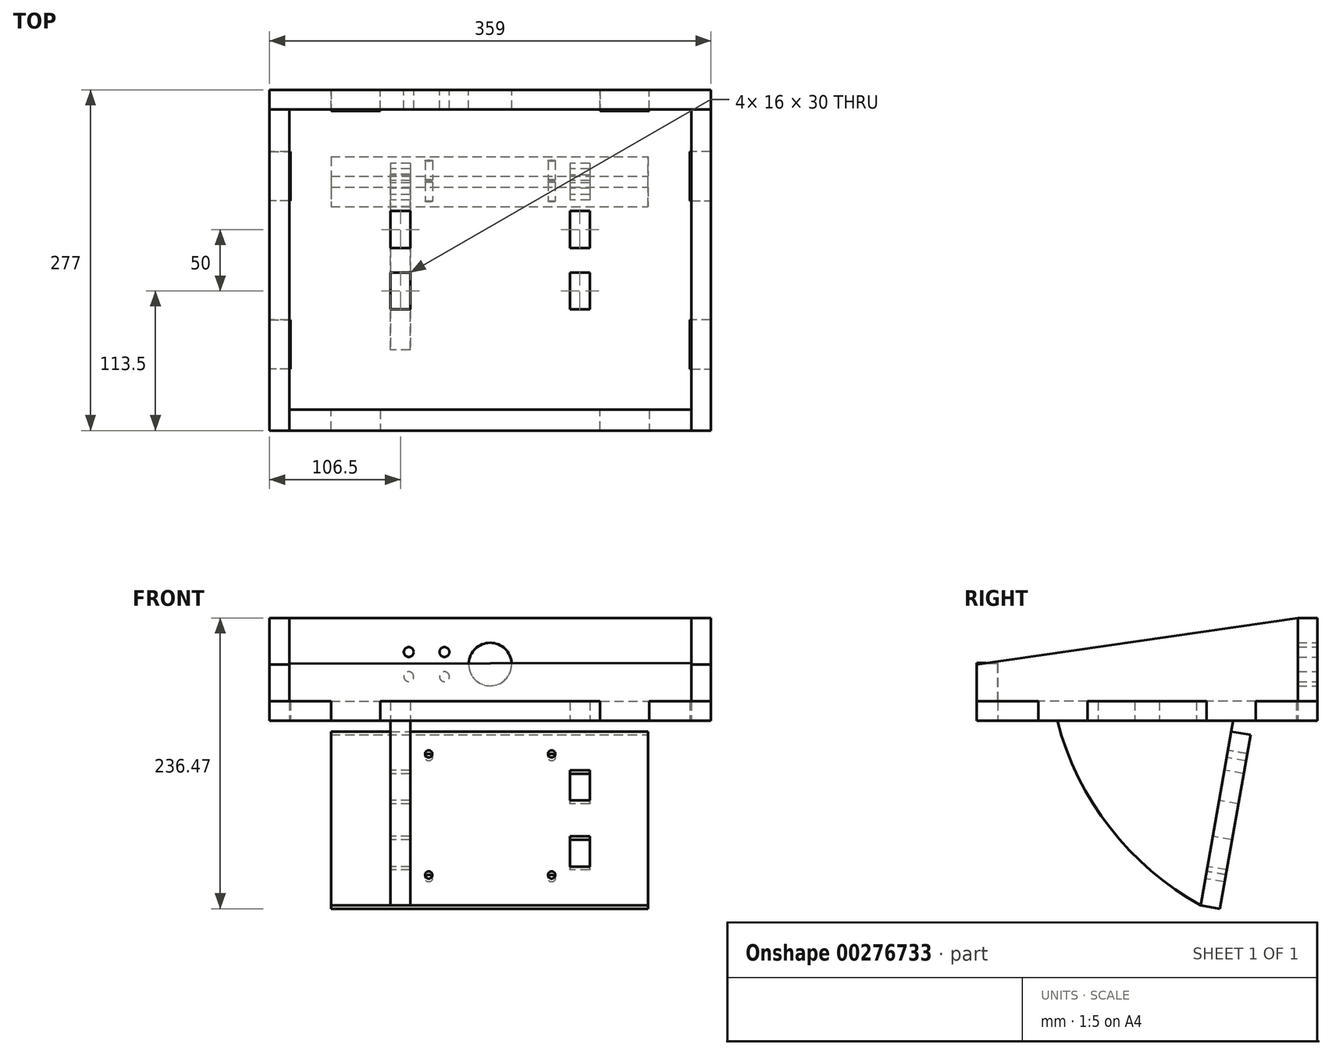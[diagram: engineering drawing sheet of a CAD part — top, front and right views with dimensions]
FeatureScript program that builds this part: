
annotation { "Feature Type Name" : "Feature", "Feature Type Description" : "" }
export const myFeature = defineFeature(function(context is Context, id is Id, definition is map)
    precondition{}
    {
        {
            var Q0;
            Q0=qCreatedBy(makeId("Top.planeOp"),FACE);
            var sketch = newSketch(context, id + "F0", { "sketchPlane" : qUnion([Q0])});
            skLineSegment(sketch, "E0.bottom", {"start": v(179.5, -138.5) * mm, "end": v(-179.5, -138.5) * mm});
            skLineSegment(sketch, "E0.top", {"start": v(179.5, 138.5) * mm, "end": v(-179.5, 138.5) * mm});
            skLineSegment(sketch, "E0.left", {"start": v(179.5, -138.5) * mm, "end": v(179.5, 138.5) * mm});
            skLineSegment(sketch, "E0.right", {"start": v(-179.5, -138.5) * mm, "end": v(-179.5, 138.5) * mm});
            skPoint(sketch, "E0.middle", {"position": v(0, 0) * mm});
            skLineSegment(sketch, "E1.bottom", {"start": v(-179.5, 138.5) * mm, "end": v(-163.5, 138.5) * mm, "construction": true});
            skLineSegment(sketch, "E1.top", {"start": v(-179.5, -138.5) * mm, "end": v(-162.5, -138.5) * mm, "construction": true});
            skLineSegment(sketch, "E1.left", {"start": v(-179.5, 138.5) * mm, "end": v(-179.5, -138.5) * mm, "construction": true});
            skLineSegment(sketch, "E2.top", {"start": v(-179.5, -138.5) * mm, "end": v(179.5, -138.5) * mm, "construction": true});
            skLineSegment(sketch, "E2.left", {"start": v(-179.5, -121.5) * mm, "end": v(-179.5, -138.5) * mm, "construction": true});
            skLineSegment(sketch, "E2.right", {"start": v(179.5, -121.5) * mm, "end": v(179.5, -138.5) * mm, "construction": true});
            skLineSegment(sketch, "E3.bottom", {"start": v(179.5, 138.5) * mm, "end": v(162.5, 138.5) * mm, "construction": true});
            skLineSegment(sketch, "E3.top", {"start": v(179.5, -138.5) * mm, "end": v(162.5, -138.5) * mm, "construction": true});
            skLineSegment(sketch, "E3.left", {"start": v(179.5, 138.5) * mm, "end": v(179.5, -138.5) * mm, "construction": true});
            skLineSegment(sketch, "E4.bottom", {"start": v(-179.5, 138.5) * mm, "end": v(179.5, 138.5) * mm, "construction": true});
            skLineSegment(sketch, "E4.left", {"start": v(-179.5, 138.5) * mm, "end": v(-179.5, 122.5) * mm, "construction": true});
            skLineSegment(sketch, "E4.right", {"start": v(179.5, 138.5) * mm, "end": v(179.5, 121.5) * mm, "construction": true});
            skLineSegment(sketch, "E5", {"start": v(-179.5, 88.5) * mm, "end": v(-162.5, 88.5) * mm});
            skLineSegment(sketch, "E6", {"start": v(-162.5, 88.5) * mm, "end": v(-162.5, 48.5) * mm});
            skLineSegment(sketch, "E7", {"start": v(-162.5, 48.5) * mm, "end": v(-179.5, 48.5) * mm});
            skLineSegment(sketch, "E8", {"start": v(-179.5, -48.5) * mm, "end": v(-162.5, -48.5) * mm});
            skLineSegment(sketch, "E9", {"start": v(-162.5, -48.5) * mm, "end": v(-162.5, -88.5) * mm});
            skLineSegment(sketch, "E10", {"start": v(-162.5, -88.5) * mm, "end": v(-179.5, -88.5) * mm});
            skLineSegment(sketch, "E11", {"start": v(-129.5, -138.5) * mm, "end": v(-129.5, -121.5) * mm});
            skLineSegment(sketch, "E12", {"start": v(-129.5, -121.5) * mm, "end": v(-89.5, -121.5) * mm});
            skLineSegment(sketch, "E13", {"start": v(-89.5, -121.5) * mm, "end": v(-89.5, -138.5) * mm});
            skLineSegment(sketch, "E14", {"start": v(89.5, -138.5) * mm, "end": v(89.5, -121.5) * mm});
            skLineSegment(sketch, "E15", {"start": v(89.5, -121.5) * mm, "end": v(129.5, -121.5) * mm});
            skLineSegment(sketch, "E16", {"start": v(129.5, -121.5) * mm, "end": v(129.5, -138.5) * mm});
            skLineSegment(sketch, "E17", {"start": v(-129.5, 138.5) * mm, "end": v(-129.5, 121.5) * mm});
            skLineSegment(sketch, "E18", {"start": v(-129.5, 121.5) * mm, "end": v(-89.5, 121.5) * mm});
            skLineSegment(sketch, "E19", {"start": v(-89.5, 121.5) * mm, "end": v(-89.5, 138.5) * mm});
            skLineSegment(sketch, "E20", {"start": v(89.5, 138.5) * mm, "end": v(89.5, 121.5) * mm});
            skLineSegment(sketch, "E21", {"start": v(89.5, 121.5) * mm, "end": v(129.5, 121.5) * mm});
            skLineSegment(sketch, "E22", {"start": v(129.5, 121.5) * mm, "end": v(129.5, 138.5) * mm});
            skLineSegment(sketch, "E23", {"start": v(179.5, 88.5) * mm, "end": v(162.5, 88.5) * mm});
            skLineSegment(sketch, "E24", {"start": v(162.5, 88.5) * mm, "end": v(162.5, 48.5) * mm});
            skLineSegment(sketch, "E25", {"start": v(162.5, 48.5) * mm, "end": v(179.5, 48.5) * mm});
            skLineSegment(sketch, "E26", {"start": v(179.5, -48.5) * mm, "end": v(162.5, -48.5) * mm});
            skLineSegment(sketch, "E27", {"start": v(162.5, -48.5) * mm, "end": v(162.5, -88.5) * mm});
            skLineSegment(sketch, "E28", {"start": v(162.5, -88.5) * mm, "end": v(179.5, -88.5) * mm});
            skSolve(sketch);
        }
        {
            var Q0;
            {var subQ11=sQuery(id+"F0.wireOp",EDGE,"E5");Q0=makeQuery(id+"F0.imprint","IMPRINT",FACE,{"disambiguationData":[TD([[makeQuery(id+"F0.imprint","IMPRINT",EDGE,{"derivedFrom":subQ11}),1.0]])]});}
            extrude(context, id + "F1", {"entities" : qUnion([Q0]), "depth" : 16 * mm});
        }
        {
            var Q0;
            {var subQ0=sQuery(id+"F0.wireOp",EDGE,"E0.right");Q0=makeQuery(id+"F1.opExtrude","SWEPT_FACE",FACE,{"disambiguationData":[OSD([subQ0]),TDD([makeQuery(id+"F0.imprint","IMPRINT",EDGE,{"disambiguationData":[TD([[makeQuery(id+"F0.imprint","INTERSECT",VERTEX,{"derivedFrom":[sQuery(id+"F0.wireOp",EDGE,"E0.top"),subQ0]}),1.0]])],"derivedFrom":subQ0})])]});}
            var sketch = newSketch(context, id + "F2", { "sketchPlane" : qUnion([Q0])});
            skLineSegment(sketch, "E29.bottom", {"start": v(-138.5, 0) * mm, "end": v(138.5, 0) * mm});
            skLineSegment(sketch, "E29.top", {"start": v(-138.5, 86) * mm, "end": v(138.5, 86) * mm});
            skLineSegment(sketch, "E29.left", {"start": v(-138.5, 0) * mm, "end": v(-138.5, 86) * mm});
            skLineSegment(sketch, "E29.right", {"start": v(138.5, 0) * mm, "end": v(138.5, 86) * mm});
            skLineSegment(sketch, "E30", {"start": v(-88.5, 0) * mm, "end": v(-88.5, 16) * mm});
            skLineSegment(sketch, "E31", {"start": v(-88.5, 16) * mm, "end": v(-48.5, 16) * mm});
            skLineSegment(sketch, "E32", {"start": v(-48.5, 16) * mm, "end": v(-48.5, 0) * mm});
            skLineSegment(sketch, "E33", {"start": v(48.5, 0) * mm, "end": v(48.5, 16) * mm});
            skLineSegment(sketch, "E34", {"start": v(48.5, 16) * mm, "end": v(88.5, 16) * mm});
            skLineSegment(sketch, "E35", {"start": v(88.5, 16) * mm, "end": v(88.5, 0) * mm});
            skLineSegment(sketch, "E36", {"start": v(-88.5, 16) * mm, "end": v(-138.5, 16) * mm});
            skLineSegment(sketch, "E37", {"start": v(-138.5, 16) * mm, "end": v(-138.5, 0) * mm});
            skLineSegment(sketch, "E38", {"start": v(-48.5, 16) * mm, "end": v(48.5, 16) * mm});
            skLineSegment(sketch, "E39", {"start": v(48.5, 0) * mm, "end": v(-48.5, 0) * mm});
            skLineSegment(sketch, "E40", {"start": v(88.5, 16) * mm, "end": v(138.5, 16) * mm});
            skLineSegment(sketch, "E41", {"start": v(138.5, 16) * mm, "end": v(138.5, 0) * mm});
            skLineSegment(sketch, "E42", {"start": v(-138.5, 86) * mm, "end": v(138.5, 46) * mm});
            skLineSegment(sketch, "E43", {"start": v(-122.5, 86) * mm, "end": v(-122.5, 83.69) * mm});
            skLineSegment(sketch, "E44", {"start": v(-122.5, 83.69) * mm, "end": v(-122.5, 16) * mm});
            skSolve(sketch);
        }
        {
            var Q0;
            {var subQ0=sQuery(id+"F2.wireOp",EDGE,"E30");Q0=makeQuery(id+"F2.imprint","IMPRINT",FACE,{"disambiguationData":[TD([[makeQuery(id+"F2.imprint","IMPRINT",EDGE,{"derivedFrom":subQ0}),1.0]])]});}
            var Q1;
            {var subQ0=sQuery(id+"F2.wireOp",EDGE,"E33");Q1=makeQuery(id+"F2.imprint","IMPRINT",FACE,{"disambiguationData":[TD([[makeQuery(id+"F2.imprint","IMPRINT",EDGE,{"derivedFrom":subQ0}),-1.0]])]});}
            var Q2;
            {var subQ0=sQuery(id+"F2.wireOp",EDGE,"E31");Q2=makeQuery(id+"F2.imprint","IMPRINT",FACE,{"disambiguationData":[TD([[makeQuery(id+"F2.imprint","IMPRINT",EDGE,{"derivedFrom":subQ0}),1.0]])]});}
            extrude(context, id + "F3", {"entities" : qUnion([Q0, Q1, Q2]), "oppositeDirection" : true, "depth" : 16 * mm});
        }
        {
            var Q0;
            {var subQ0=sQuery(id+"F0.wireOp",EDGE,"E0.top");Q0=makeQuery(id+"F1.opExtrude","SWEPT_FACE",FACE,{"disambiguationData":[OSD([subQ0]),TDD([makeQuery(id+"F0.imprint","IMPRINT",EDGE,{"disambiguationData":[TD([[makeQuery(id+"F0.imprint","INTERSECT",VERTEX,{"derivedFrom":[subQ0,sQuery(id+"F0.wireOp",EDGE,"E0.left")]}),-1.0]])],"derivedFrom":subQ0})])]});}
            var sketch = newSketch(context, id + "F4", { "sketchPlane" : qUnion([Q0])});
            skLineSegment(sketch, "E45", {"start": v(179.5, 16) * mm, "end": v(129.5, 16) * mm});
            skLineSegment(sketch, "E46", {"start": v(129.5, 16) * mm, "end": v(129.5, 0) * mm});
            skLineSegment(sketch, "E47", {"start": v(129.5, 0) * mm, "end": v(89.35, 0) * mm});
            skLineSegment(sketch, "E48", {"start": v(89.35, 0) * mm, "end": v(89.35, 16) * mm});
            skLineSegment(sketch, "E49", {"start": v(89.35, 16) * mm, "end": v(-89.5, 16) * mm});
            skLineSegment(sketch, "E50", {"start": v(-89.5, 16) * mm, "end": v(-89.5, 0) * mm});
            skLineSegment(sketch, "E51", {"start": v(-89.5, 0) * mm, "end": v(-129.5, 0) * mm});
            skLineSegment(sketch, "E52", {"start": v(-129.5, 0) * mm, "end": v(-129.5, 16) * mm});
            skLineSegment(sketch, "E53", {"start": v(-129.5, 16) * mm, "end": v(-179.5, 16) * mm});
            skLineSegment(sketch, "E54", {"start": v(-179.5, 16) * mm, "end": v(-179.5, 83.69) * mm});
            skLineSegment(sketch, "E55", {"start": v(-179.5, 83.69) * mm, "end": v(179.5, 83.69) * mm});
            skLineSegment(sketch, "E56", {"start": v(179.5, 83.69) * mm, "end": v(179.5, 16) * mm});
            skSolve(sketch);
        }
        {
            var Q0;
            Q0=makeQuery(id+"F4.imprint","IMPRINT",FACE,{"disambiguationData":[TD([[makeQuery(id+"F4.imprint","IMPRINT",EDGE,{"derivedFrom":sQuery(id+"F4.wireOp",EDGE,"E45")}),-1.0]])]});
            extrude(context, id + "F5", {"entities" : qUnion([Q0]), "oppositeDirection" : true, "depth" : 16 * mm});
        }
        {
            var Q0;
            {var subQ0=sQuery(id+"F0.wireOp",EDGE,"E0.left");Q0=makeQuery(id+"F1.opExtrude","SWEPT_FACE",FACE,{"disambiguationData":[OSD([subQ0]),TDD([makeQuery(id+"F0.imprint","IMPRINT",EDGE,{"disambiguationData":[TD([[makeQuery(id+"F0.imprint","INTERSECT",VERTEX,{"derivedFrom":[sQuery(id+"F0.wireOp",EDGE,"E0.bottom"),subQ0]}),-1.0]])],"derivedFrom":subQ0})])]});}
            var sketch = newSketch(context, id + "F6", { "sketchPlane" : qUnion([Q0])});
            skLineSegment(sketch, "E57", {"start": v(-138.5, 16) * mm, "end": v(-138.5, 46) * mm});
            skLineSegment(sketch, "E58", {"start": v(-88.5, 16) * mm, "end": v(-88.5, 0) * mm});
            skLineSegment(sketch, "E59", {"start": v(-88.5, 0) * mm, "end": v(-48.5, 0) * mm});
            skLineSegment(sketch, "E60", {"start": v(-48.5, 0) * mm, "end": v(-48.5, 16) * mm});
            skLineSegment(sketch, "E61", {"start": v(-48.5, 16) * mm, "end": v(48.5, 16) * mm});
            skLineSegment(sketch, "E62", {"start": v(48.5, 16) * mm, "end": v(48.5, 0) * mm});
            skLineSegment(sketch, "E63", {"start": v(48.5, 0) * mm, "end": v(88.5, 0) * mm});
            skLineSegment(sketch, "E64", {"start": v(88.5, 0) * mm, "end": v(88.5, 16) * mm});
            skLineSegment(sketch, "E65", {"start": v(88.5, 16) * mm, "end": v(122.5, 16) * mm});
            skLineSegment(sketch, "E66", {"start": v(122.5, 16) * mm, "end": v(122.5, 83.69) * mm});
            skLineSegment(sketch, "E67", {"start": v(122.5, 83.69) * mm, "end": v(-138.5, 46) * mm});
            skSolve(sketch);
        }
        {
            var Q0;
            Q0=makeQuery(id+"F6.imprint","IMPRINT",FACE,{"disambiguationData":[TD([[makeQuery(id+"F6.imprint","IMPRINT",EDGE,{"derivedFrom":sQuery(id+"F6.wireOp",EDGE,"E57")}),-1.0]])]});
            extrude(context, id + "F7", {"entities" : qUnion([Q0]), "oppositeDirection" : true, "depth" : 16 * mm});
        }
        {
            var Q0;
            {var subQ0=sQuery(id+"F0.wireOp",EDGE,"E0.bottom");Q0=makeQuery(id+"F1.opExtrude","SWEPT_FACE",FACE,{"disambiguationData":[OSD([subQ0]),TDD([makeQuery(id+"F0.imprint","IMPRINT",EDGE,{"disambiguationData":[TD([[makeQuery(id+"F0.imprint","INTERSECT",VERTEX,{"derivedFrom":[subQ0,sQuery(id+"F0.wireOp",EDGE,"E0.right")]}),1.0]])],"derivedFrom":subQ0})])]});}
            var sketch = newSketch(context, id + "F8", { "sketchPlane" : qUnion([Q0])});
            skLineSegment(sketch, "E68", {"start": v(-163.5, 46.6) * mm, "end": v(-163.5, 16) * mm});
            skLineSegment(sketch, "E69", {"start": v(-163.5, 16) * mm, "end": v(-129.5, 16) * mm});
            skLineSegment(sketch, "E70", {"start": v(-129.5, 16) * mm, "end": v(-129.5, 0) * mm});
            skLineSegment(sketch, "E71", {"start": v(-129.5, 0) * mm, "end": v(-89.5, 0) * mm});
            skLineSegment(sketch, "E72", {"start": v(-89.5, 0) * mm, "end": v(-89.5, 16) * mm});
            skLineSegment(sketch, "E73", {"start": v(-89.5, 16) * mm, "end": v(89.5, 16) * mm});
            skLineSegment(sketch, "E74", {"start": v(89.5, 16) * mm, "end": v(89.5, 0) * mm});
            skLineSegment(sketch, "E75", {"start": v(89.5, 0) * mm, "end": v(129.5, 0) * mm});
            skLineSegment(sketch, "E76", {"start": v(129.5, 0) * mm, "end": v(129.5, 16) * mm});
            skLineSegment(sketch, "E77", {"start": v(129.5, 16) * mm, "end": v(163.5, 16) * mm});
            skLineSegment(sketch, "E78", {"start": v(163.5, 16) * mm, "end": v(163.5, 47.06) * mm});
            skLineSegment(sketch, "E79", {"start": v(163.5, 47.06) * mm, "end": v(-163.5, 46.6) * mm});
            skSolve(sketch);
        }
        {
            var Q0;
            Q0 = qSketchRegion(id + "F8", true);
            extrude(context, id + "F9", {"entities" : qUnion([Q0]), "oppositeDirection" : true, "depth" : 17 * mm});
        }
        {
            var Q0;
            Q0=makeQuery(id+"F5.opExtrude","CAP_FACE",FACE,{"disambiguationData":[OSD([sQuery(id+"F4.wireOp",EDGE,"E45"),sQuery(id+"F4.wireOp",EDGE,"E46"),sQuery(id+"F4.wireOp",EDGE,"E47"),sQuery(id+"F4.wireOp",EDGE,"E48"),sQuery(id+"F4.wireOp",EDGE,"E49"),sQuery(id+"F4.wireOp",EDGE,"E50"),sQuery(id+"F4.wireOp",EDGE,"E51"),sQuery(id+"F4.wireOp",EDGE,"E52"),sQuery(id+"F4.wireOp",EDGE,"E53"),sQuery(id+"F4.wireOp",EDGE,"E54"),sQuery(id+"F4.wireOp",EDGE,"E55"),sQuery(id+"F4.wireOp",EDGE,"E56")])],"isStart":true});
            var sketch = newSketch(context, id + "F10", { "sketchPlane" : qUnion([Q0])});
            skCircle(sketch, "E80", {"center": v(0, 46) * mm, "radius": 17.5 * mm});
            skCircle(sketch, "E81", {"center": v(37.22, 56) * mm, "radius": 4 * mm});
            skCircle(sketch, "E82", {"center": v(37.22, 36) * mm, "radius": 4 * mm});
            skCircle(sketch, "E83", {"center": v(66.21, 56) * mm, "radius": 4 * mm});
            skCircle(sketch, "E84", {"center": v(66.21, 36) * mm, "radius": 4 * mm});
            skLineSegment(sketch, "E85", {"start": v(0, 46) * mm, "end": v(95.92, 46) * mm, "construction": true});
            skSolve(sketch);
        }
        {
            var Q0;
            Q0=makeQuery(id+"F10.imprint","IMPRINT",FACE,{"disambiguationData":[TD([[makeQuery(id+"F10.imprint","IMPRINT",EDGE,{"derivedFrom":sQuery(id+"F10.wireOp",EDGE,"E80")}),1.0]])]});
            var Q1;
            Q1=makeQuery(id+"F10.imprint","IMPRINT",FACE,{"disambiguationData":[TD([[makeQuery(id+"F10.imprint","IMPRINT",EDGE,{"derivedFrom":sQuery(id+"F10.wireOp",EDGE,"E81")}),1.0]])]});
            var Q2;
            Q2=makeQuery(id+"F10.imprint","IMPRINT",FACE,{"disambiguationData":[TD([[makeQuery(id+"F10.imprint","IMPRINT",EDGE,{"derivedFrom":sQuery(id+"F10.wireOp",EDGE,"E83")}),1.0]])]});
            var Q3;
            Q3=makeQuery(id+"F10.imprint","IMPRINT",FACE,{"disambiguationData":[TD([[makeQuery(id+"F10.imprint","IMPRINT",EDGE,{"derivedFrom":sQuery(id+"F10.wireOp",EDGE,"E84")}),1.0]])]});
            var Q4;
            Q4=makeQuery(id+"F10.imprint","IMPRINT",FACE,{"disambiguationData":[TD([[makeQuery(id+"F10.imprint","IMPRINT",EDGE,{"derivedFrom":sQuery(id+"F10.wireOp",EDGE,"E82")}),1.0]])]});
            extrude(context, id + "F11", {"entities" : qUnion([Q0, Q1, Q2, Q3, Q4]), "operationType" : NewBodyOperationType.REMOVE, "oppositeDirection" : true, "depth" : 25 * mm});
        }
        {
            var Q0;
            Q0=makeQuery(id+"F1.opExtrude","CAP_FACE",FACE,{"disambiguationData":[OSD([sQuery(id+"F0.wireOp",EDGE,"E0.bottom"),sQuery(id+"F0.wireOp",EDGE,"E0.top"),sQuery(id+"F0.wireOp",EDGE,"E0.left"),sQuery(id+"F0.wireOp",EDGE,"E0.right"),sQuery(id+"F0.wireOp",EDGE,"E5"),sQuery(id+"F0.wireOp",EDGE,"E6"),sQuery(id+"F0.wireOp",EDGE,"E7"),sQuery(id+"F0.wireOp",EDGE,"E8"),sQuery(id+"F0.wireOp",EDGE,"E9"),sQuery(id+"F0.wireOp",EDGE,"E10"),sQuery(id+"F0.wireOp",EDGE,"E11"),sQuery(id+"F0.wireOp",EDGE,"E12"),sQuery(id+"F0.wireOp",EDGE,"E13"),sQuery(id+"F0.wireOp",EDGE,"E14"),sQuery(id+"F0.wireOp",EDGE,"E15"),sQuery(id+"F0.wireOp",EDGE,"E16"),sQuery(id+"F0.wireOp",EDGE,"E17"),sQuery(id+"F0.wireOp",EDGE,"E18"),sQuery(id+"F0.wireOp",EDGE,"E19"),sQuery(id+"F0.wireOp",EDGE,"E20"),sQuery(id+"F0.wireOp",EDGE,"E21"),sQuery(id+"F0.wireOp",EDGE,"E22"),sQuery(id+"F0.wireOp",EDGE,"E23"),sQuery(id+"F0.wireOp",EDGE,"E24"),sQuery(id+"F0.wireOp",EDGE,"E25"),sQuery(id+"F0.wireOp",EDGE,"E26"),sQuery(id+"F0.wireOp",EDGE,"E27"),sQuery(id+"F0.wireOp",EDGE,"E28")])],"isStart":true});
            var sketch = newSketch(context, id + "F12", { "sketchPlane" : qUnion([Q0])});
            skLineSegment(sketch, "E86.bottom", {"start": v(81, -40) * mm, "end": v(65, -40) * mm});
            skLineSegment(sketch, "E86.top", {"start": v(81, -10) * mm, "end": v(65, -10) * mm});
            skLineSegment(sketch, "E86.left", {"start": v(81, -40) * mm, "end": v(81, -10) * mm});
            skLineSegment(sketch, "E86.right", {"start": v(65, -40) * mm, "end": v(65, -10) * mm});
            skLineSegment(sketch, "E87.bottom", {"start": v(81, 10) * mm, "end": v(65, 10) * mm});
            skLineSegment(sketch, "E87.top", {"start": v(81, 40) * mm, "end": v(65, 40) * mm});
            skLineSegment(sketch, "E87.left", {"start": v(81, 10) * mm, "end": v(81, 40) * mm});
            skLineSegment(sketch, "E87.right", {"start": v(65, 10) * mm, "end": v(65, 40) * mm});
            skLineSegment(sketch, "E88.bottom", {"start": v(-65, -40) * mm, "end": v(-81, -40) * mm});
            skLineSegment(sketch, "E88.top", {"start": v(-65, -10) * mm, "end": v(-81, -10) * mm});
            skLineSegment(sketch, "E88.left", {"start": v(-65, -40) * mm, "end": v(-65, -10) * mm});
            skLineSegment(sketch, "E88.right", {"start": v(-81, -40) * mm, "end": v(-81, -10) * mm});
            skLineSegment(sketch, "E89.bottom", {"start": v(-65, 10) * mm, "end": v(-81, 10) * mm});
            skLineSegment(sketch, "E89.top", {"start": v(-65, 40) * mm, "end": v(-81, 40) * mm});
            skLineSegment(sketch, "E89.left", {"start": v(-65, 10) * mm, "end": v(-65, 40) * mm});
            skLineSegment(sketch, "E89.right", {"start": v(-81, 10) * mm, "end": v(-81, 40) * mm});
            skSolve(sketch);
        }
        {
            var Q0;
            Q0 = qSketchRegion(id + "F12", true);
            extrude(context, id + "F13", {"entities" : qUnion([Q0]), "operationType" : NewBodyOperationType.REMOVE, "oppositeDirection" : true, "depth" : 25 * mm});
        }
        {
            var Q0;
            Q0=makeQuery(id+"F13.boolean.opBoolean","COPY",FACE,{"derivedFrom":makeQuery(id+"F13.opExtrude","SWEPT_FACE",FACE,{"disambiguationData":[OSD([sQuery(id+"F12.wireOp",EDGE,"E89.right")])]})});
            var sketch = newSketch(context, id + "F14", { "sketchPlane" : qUnion([Q0])});
            skLineSegment(sketch, "E90", {"start": v(-40, 16) * mm, "end": v(-40, 0) * mm});
            skLineSegment(sketch, "E91", {"start": v(-40, 0) * mm, "end": v(-73.05, 0) * mm});
            skLineSegment(sketch, "E92", {"start": v(-73.05, 0) * mm, "end": v(-73.05, -150) * mm});
            skLineSegment(sketch, "E93", {"start": v(-73.05, -150) * mm, "end": v(43.55, -150) * mm});
            skLineSegment(sketch, "E94", {"start": v(43.55, -150) * mm, "end": v(70, 0) * mm});
            skLineSegment(sketch, "E95", {"start": v(70, 0) * mm, "end": v(40, 0) * mm});
            skLineSegment(sketch, "E96", {"start": v(40, 0) * mm, "end": v(40, 16) * mm});
            skLineSegment(sketch, "E97", {"start": v(40, 16) * mm, "end": v(9.89, 16) * mm});
            skLineSegment(sketch, "E98", {"start": v(9.89, 16) * mm, "end": v(9.89, 0) * mm});
            skLineSegment(sketch, "E99", {"start": v(9.89, 0) * mm, "end": v(-10, 0) * mm});
            skLineSegment(sketch, "E100", {"start": v(-10, 0) * mm, "end": v(-10, 16) * mm});
            skLineSegment(sketch, "E101", {"start": v(-10, 16) * mm, "end": v(-40, 16) * mm});
            skLineSegment(sketch, "E102", {"start": v(62.92, -40.15) * mm, "end": v(78.68, -42.93) * mm});
            skLineSegment(sketch, "E103", {"start": v(78.68, -42.93) * mm, "end": v(74.34, -67.55) * mm});
            skLineSegment(sketch, "E104", {"start": v(74.34, -67.55) * mm, "end": v(58.58, -64.77) * mm});
            skLineSegment(sketch, "E105", {"start": v(58.58, -64.77) * mm, "end": v(53.45, -93.87) * mm});
            skLineSegment(sketch, "E106", {"start": v(53.45, -93.87) * mm, "end": v(69.2, -96.64) * mm});
            skLineSegment(sketch, "E107", {"start": v(69.2, -96.64) * mm, "end": v(64.86, -121.26) * mm});
            skLineSegment(sketch, "E108", {"start": v(64.86, -121.26) * mm, "end": v(49.1, -118.49) * mm});
            skArc(sketch, "E109", {"start": v(-73.05, 0) * mm, "mid": v(-30.2, -87) * mm, "end": v(43.55, -150) * mm});
            skSolve(sketch);
        }
        {
            var Q0;
            Q0=makeQuery(id+"F14.imprint","IMPRINT",FACE,{"disambiguationData":[TD([[makeQuery(id+"F14.imprint","IMPRINT",EDGE,{"derivedFrom":sQuery(id+"F14.wireOp",EDGE,"E90")}),1.0]])]});
            var Q1;
            {var subQ0=sQuery(id+"F14.wireOp",EDGE,"E106");Q1=makeQuery(id+"F14.imprint","IMPRINT",FACE,{"disambiguationData":[TD([[makeQuery(id+"F14.imprint","IMPRINT",EDGE,{"derivedFrom":subQ0}),-1.0]])]});}
            var Q2;
            {var subQ0=sQuery(id+"F14.wireOp",EDGE,"E102");Q2=makeQuery(id+"F14.imprint","IMPRINT",FACE,{"disambiguationData":[TD([[makeQuery(id+"F14.imprint","IMPRINT",EDGE,{"derivedFrom":subQ0}),-1.0]])]});}
            var Q3;
            Q3=makeQuery(id+"F14.imprint","IMPRINT",FACE,{"disambiguationData":[TD([[makeQuery(id+"F14.imprint","IMPRINT",EDGE,{"derivedFrom":sQuery(id+"F14.wireOp",EDGE,"E91")}),1.0]])]});
            extrude(context, id + "F15", {"entities" : qUnion([Q0, Q1, Q2, Q3]), "depth" : 16 * mm});
        }
        {
            var Q0;
            Q0=makeQuery(id+"F15.opExtrude","SWEPT_FACE",FACE,{"disambiguationData":[OSD([sQuery(id+"F14.wireOp",EDGE,"E94")])]});
            var sketch = newSketch(context, id + "F16", { "sketchPlane" : qUnion([Q0])});
            skLineSegment(sketch, "E110.bottom", {"start": v(129.5, 3.39) * mm, "end": v(-128.5, 3.39) * mm});
            skLineSegment(sketch, "E110.top", {"start": v(129.5, -140.16) * mm, "end": v(-128.5, -140.16) * mm});
            skLineSegment(sketch, "E110.left", {"start": v(129.5, 3.39) * mm, "end": v(129.5, -140.16) * mm});
            skLineSegment(sketch, "E110.right", {"start": v(-128.5, -140.16) * mm, "end": v(-128.5, 3.39) * mm});
            skCircle(sketch, "E111", {"center": v(-50, -15.16) * mm, "radius": 3 * mm});
            skCircle(sketch, "E112", {"center": v(50, -15.16) * mm, "radius": 3 * mm});
            skCircle(sketch, "E113", {"center": v(-50, -115.16) * mm, "radius": 3 * mm});
            skCircle(sketch, "E114", {"center": v(50, -115.16) * mm, "radius": 3 * mm});
            skLineSegment(sketch, "E115.bottom", {"start": v(65, -28.61) * mm, "end": v(81, -28.61) * mm});
            skLineSegment(sketch, "E115.top", {"start": v(65, -53.61) * mm, "end": v(81, -53.61) * mm});
            skLineSegment(sketch, "E115.left", {"start": v(65, -28.61) * mm, "end": v(65, -53.61) * mm});
            skLineSegment(sketch, "E115.right", {"start": v(81, -28.61) * mm, "end": v(81, -53.61) * mm});
            skLineSegment(sketch, "E116.bottom", {"start": v(65, -83.16) * mm, "end": v(81, -83.16) * mm});
            skLineSegment(sketch, "E116.top", {"start": v(65, -108.16) * mm, "end": v(81, -108.16) * mm});
            skLineSegment(sketch, "E116.left", {"start": v(65, -83.16) * mm, "end": v(65, -108.16) * mm});
            skLineSegment(sketch, "E116.right", {"start": v(81, -83.16) * mm, "end": v(81, -108.16) * mm});
            skLineSegment(sketch, "E117.bottom", {"start": v(-81, -28.61) * mm, "end": v(-65, -28.61) * mm});
            skLineSegment(sketch, "E117.top", {"start": v(-81, -53.61) * mm, "end": v(-65, -53.61) * mm});
            skLineSegment(sketch, "E117.left", {"start": v(-81, -28.61) * mm, "end": v(-81, -53.61) * mm});
            skLineSegment(sketch, "E117.right", {"start": v(-65, -28.61) * mm, "end": v(-65, -53.61) * mm});
            skLineSegment(sketch, "E118.bottom", {"start": v(-81, -83.16) * mm, "end": v(-65, -83.16) * mm});
            skLineSegment(sketch, "E118.top", {"start": v(-81, -108.16) * mm, "end": v(-65, -108.16) * mm});
            skLineSegment(sketch, "E118.left", {"start": v(-81, -83.16) * mm, "end": v(-81, -108.16) * mm});
            skLineSegment(sketch, "E118.right", {"start": v(-65, -83.16) * mm, "end": v(-65, -108.16) * mm});
            skLineSegment(sketch, "E119", {"start": v(-128.5, 3.39) * mm, "end": v(-128.5, -140.16) * mm});
            skLineSegment(sketch, "E120", {"start": v(-128.5, -140.16) * mm, "end": v(129.5, -140.16) * mm});
            skLineSegment(sketch, "E121", {"start": v(129.5, -140.16) * mm, "end": v(129.5, 3.39) * mm});
            skSolve(sketch);
        }
        {
            var Q0;
            Q0 = qSketchRegion(id + "F16", true);
            extrude(context, id + "F17", {"entities" : qUnion([Q0]), "depth" : 16 * mm});
        }
    });
